# Revit family: HOSPIVAC 2 SIRELLA
name_source: partatom
category: Equipement de génie climatique
revit_build: Autodesk Revit 2018 (Build: 20170223_1515(x64)
units: mm (PartAtom-declared; Revit-internal decimal feet)

## family parameters
Basée sur le plan de construction = Non
Classification = Aucun
Cote de connecteur circulaire = Utiliser le diamètre
Couper avec des vides une fois chargée = Non
Partagée = Non
Point de calcul de pièce = Non
Toujours verticalement = Oui
Type d'élément = Normal

## types (3) — shared parameters
ANGLE = 60.00°
BRANCHEMENT_TERRE = Oui
COS_PHI = 0.9
DESCR_ALIM_X = Alimentation X ; 4G2.5mm²
DESCR_ALIM_Y = Alimentation Y ; 4G2.5mm²
DOUBLE_ALIMENTATION = Oui
ENTRAXE_ALIM_ELEC = 526 mm
ENTRAXE_CANA_ASPI = 900 mm
EP.VIROLE = 3 mm  [stored 0.00984252 ft]
Fabricant = MIL'S
HAUT_ASPI = 60 mm  [stored 0.19685 ft]
HAUT_CANA_FILTRE = 30 mm  [stored 0.0984252 ft]
HAUT_REFOUL = 1520 mm
HAUT_TETE_FILTRE = 104 mm
HAUT_VIROLE = 155 mm  [stored 0.50853 ft]
LARGEUR = 1100 mm
LG_VIROLE = 2000 mm
LONGUEUR = 2400 mm
LONG_ENTRAXE_PIED = 1500 mm
LONG_FOND = 145 mm
LONG_OFFSET_REFOUL = 220 mm  [stored 0.721785 ft]
LONG_SELLETTE_1 = 1995 mm
Lien espace client = https://www.mils.fr
Modèle = HOSPIVAC
NBR_POLES = 3
NEUTRE = Oui
OFFSET2_LARG_ZONE_MAINT = 625 mm
OFFSET_CENTRAGE_PPE = 200 mm  [stored 0.656168 ft]
OFFSET_COUDE_CANA_FILTRE = 230 mm
OFFSET_HAUT_CANA_REFOUL = 820 mm
OFFSET_HAUT_FILTRE = 725 mm
OFFSET_HAUT_SELLETTE = 860 mm
OFFSET_LARG_ASPI_PPE = 150 mm
OFFSET_LARG_CANA_REFOUL = 294.5 mm
OFFSET_LARG_FILTRE = 410 mm
OFFSET_LARG_REFOUL = 503.5 mm
OFFSET_LONG_ASPI = 221 mm  [stored 0.725066 ft]
OFFSET_LONG_CANA_REFOUL = 1823 mm
OFFSET_LONG_FILTRE1 = 650 mm
OFFSET_LONG_FILTRE2 = 40 mm  [stored 0.131234 ft]
OFFSET_LONG_REFOUL = 945 mm
OFFSET_LONG_REFOUL_PPE_A = 945 mm
OFFSET_PPE = 40 mm  [stored 0.131234 ft]
OFFSET_SELLETTE_1 = 55 mm  [stored 0.180446 ft]
TENSION_ALIM = 400 V
ØVIROLE = 650 mm

## per-type parameters (varying)
- b - HOSPIVAC 2 SL150.R: DEBIT_ASPI_VIDE=280.0 m³/h; DEBIT_REFOUL_VIDE=280.0 m³/h; DESCR_ASPI=Aspiration Vide ; 2x140 m³/h ; G 1"1/2 FEM; DESCR_REFOUL=Refoulement Vide ; 2x140 m³/h ; G 1"1/2"FEM; DIAM_ASPI_VIDE=40 mm  [stored 0.131234 ft]; DIAM_REFOUL_VIDE=40 mm  [stored 0.131234 ft]; HAUTEUR=1500 mm; HAUT_CANA_ASPI=1500 mm; HAUT_CANA_REFOUL=124 mm; HAUT_FILTRE=380 mm; HAUT_FIX=15.2 mm; HAUT_REFOUL_PPE=949.8 mm; LONG_CANA_REFOUL=190.1 mm; LONG_REFOUL=65.2 mm  [stored 0.213911 ft]; LONG_U=650 mm; NIVEAU_SONORE(dB(A))=69; OFFSET1_LARG_ZONE_MAINT=697.5 mm; OFFSET_BRIDE=200 mm  [stored 0.656168 ft]; OFFSET_LARG_1=182 mm  [stored 0.597113 ft]; OFFSET_LARG_2=332 mm; OFFSET_LONG_A1=377 mm  [stored 1.23688 ft]; OFFSET_LONG_A2=637 mm; OFFSET_LONG_B1=1277 mm; OFFSET_LONG_B2=1537 mm; OFFSET_LONG_CANA_ASPI=597 mm; OFFSET_LONG_CANA_REFOUL_PPE_B=162.1 mm; OFFSET_REFOUL_PPE_A=1001.1 mm; OFFSET_REFOUL_PPE_B=221.7 mm  [stored 0.727362 ft]; POIDS(Kg)=670 mm; PUISS_APPARENTE=3333 VA; PUISS_APPARENTE_2=3333 VA; PUISS_ELECT=3 kW; PUISS_ELECT_2=3 kW; TAILLE_POMPE=SIRELLA SLR : SL150.R; ØCANA=40 mm  [stored 0.131234 ft]; ØFILTRE=195 mm; ØPOT_FILTRE=150 mm
- a - HOSPIVAC 2 SL100.R: DEBIT_ASPI_VIDE=180.0 m³/h; DEBIT_REFOUL_VIDE=180.0 m³/h; DESCR_ASPI=Aspiration Vide ; 2x90 m³/h ; G 1"1/2FEM; DESCR_REFOUL=Refoulement Vide ; 2x90 m³/h ; G 1"1/2"FEM; DIAM_ASPI_VIDE=32 mm  [stored 0.104987 ft]; DIAM_REFOUL_VIDE=32 mm  [stored 0.104987 ft]; HAUTEUR=1500 mm; HAUT_CANA_ASPI=1500 mm; HAUT_CANA_REFOUL=124 mm; HAUT_FILTRE=425 mm; HAUT_FIX=15.2 mm; HAUT_REFOUL_PPE=949.8 mm; LONG_CANA_REFOUL=190.1 mm; LONG_REFOUL=65.2 mm  [stored 0.213911 ft]; LONG_U=650 mm; NIVEAU_SONORE(dB(A))=69; OFFSET1_LARG_ZONE_MAINT=656 mm; OFFSET_BRIDE=200.5 mm  [stored 0.657808 ft]; OFFSET_LARG_1=182 mm  [stored 0.597113 ft]; OFFSET_LARG_2=332 mm; OFFSET_LONG_A1=377 mm  [stored 1.23688 ft]; OFFSET_LONG_A2=637 mm; OFFSET_LONG_B1=1277 mm; OFFSET_LONG_B2=1537 mm; OFFSET_LONG_CANA_ASPI=597 mm; OFFSET_LONG_CANA_REFOUL_PPE_B=162.1 mm; OFFSET_REFOUL_PPE_A=1001.1 mm; OFFSET_REFOUL_PPE_B=221.7 mm  [stored 0.727362 ft]; POIDS(Kg)=650 mm; PUISS_APPARENTE=2444 VA; PUISS_APPARENTE_2=2444 VA; PUISS_ELECT=2 kW; PUISS_ELECT_2=2 kW; TAILLE_POMPE=SIRELLA SLR : SL100.R; ØCANA=40 mm  [stored 0.131234 ft]; ØFILTRE=112 mm; ØPOT_FILTRE=100 mm  [stored 0.328084 ft]
- c - HOSPIVAC 2 SL300.R: DEBIT_ASPI_VIDE=520.0 m³/h; DEBIT_REFOUL_VIDE=520.0 m³/h; DESCR_ASPI=Aspiration Vide ; 2x260 m³/h ; G 2"FEM; DESCR_REFOUL=Refoulement Vide ; 2x260 m³/h ; G 2"FEM; DIAM_ASPI_VIDE=50 mm  [stored 0.164042 ft]; DIAM_REFOUL_VIDE=50 mm  [stored 0.164042 ft]; HAUTEUR=1600 mm; HAUT_CANA_ASPI=1550 mm; HAUT_CANA_REFOUL=139 mm; HAUT_FILTRE=380 mm; HAUT_FIX=24.4 mm  [stored 0.0800525 ft]; HAUT_REFOUL_PPE=950 mm; LONG_CANA_REFOUL=195 mm; LONG_REFOUL=80 mm  [stored 0.262467 ft]; LONG_U=730 mm; NIVEAU_SONORE(dB(A))=70; OFFSET1_LARG_ZONE_MAINT=697.5 mm; OFFSET_BRIDE=266.5 mm; OFFSET_LARG_1=251 mm  [stored 0.823491 ft]; OFFSET_LARG_2=401 mm; OFFSET_LONG_A1=337 mm; OFFSET_LONG_A2=597 mm; OFFSET_LONG_B1=1237 mm; OFFSET_LONG_B2=1497 mm; OFFSET_LONG_CANA_ASPI=559 mm; OFFSET_LONG_CANA_REFOUL_PPE_B=192.6 mm; OFFSET_REFOUL_PPE_A=974.7 mm; OFFSET_REFOUL_PPE_B=195.2 mm; POIDS(Kg)=940 mm; PUISS_APPARENTE=6111 VA; PUISS_APPARENTE_2=6111 VA; PUISS_ELECT=6 kW; PUISS_ELECT_2=6 kW; TAILLE_POMPE=SIRELLA SLR : SL300.R; ØCANA=50 mm  [stored 0.164042 ft]; ØFILTRE=195 mm; ØPOT_FILTRE=150 mm

note: [stored X ft] marks values corroborated as IEEE doubles in the binary element streams (Revit-internal decimal feet)
